FCSTD DOCUMENT  (FreeCAD 1.0R39319 (Git))
Label: session2_drawing4
License: All rights reserved
LicenseURL: https://en.wikipedia.org/wiki/All_rights_reserved
objects: Sketcher::SketchObject×1, PartDesign::Body×1
note: 3 computed .brp shape members not serialized (recipe doc carries the construction recipe); baked Part::Feature solids carry a one-line shape summary decoded from their .brp

FEATURE [Sketcher::SketchObject] Sketch
  ArcFitTolerance = 1e-06
  AttachmentSupport = -> [XY_Plane]
  FullyConstrained = true
  MakeInternals = false
  MapMode = 5
  sketch-geometry (32):
    g0: ArcOfCircle CenterX=-6.783e-13 CenterY=2.02e-13 CenterZ=0 NormalX=0 NormalY=0 NormalZ=1 AngleXU=0 Radius=55 StartAngle=1.75363 EndAngle=2.95876
    g1: ArcOfCircle CenterX=-113 CenterY=1.8543e-12 CenterZ=0 NormalX=0 NormalY=0 NormalZ=1 AngleXU=0 Radius=26 StartAngle=0.394791 EndAngle=5.88839
    g2: ArcOfCircle CenterX=113 CenterY=4.685e-13 CenterZ=0 NormalX=0 NormalY=0 NormalZ=1 AngleXU=0 Radius=26 StartAngle=3.53638 EndAngle=9.02999
    g3: ArcOfCircle CenterX=5.801e-13 CenterY=113 CenterZ=0 NormalX=0 NormalY=0 NormalZ=1 AngleXU=0 Radius=26 StartAngle=5.10718 EndAngle=10.6008
    g4: LineSegment StartX=-131.385 StartY=18.3848 StartZ=0 EndX=-18.3848 EndY=131.385 EndZ=0
    g5: LineSegment StartX=18.3848 StartY=131.385 StartZ=0 EndX=131.385 EndY=18.3848 EndZ=0
    g6: ArcOfCircle CenterX=8.066e-13 CenterY=-113 CenterZ=0 NormalX=0 NormalY=0 NormalZ=1 AngleXU=0 Radius=26 StartAngle=1.96559 EndAngle=7.45919
    g7: Circle [constr] CenterX=-6.783e-13 CenterY=2.02e-13 CenterZ=0 NormalX=0 NormalY=0 NormalZ=1 AngleXU=0 Radius=113
    g8: ArcOfCircle CenterX=-59.8055 CenterY=-85.0841 CenterZ=0 NormalX=0 NormalY=0 NormalZ=1 AngleXU=0 Radius=40 StartAngle=5.84647 EndAngle=7.24131
    g9: ArcOfCircle CenterX=-6.783e-13 CenterY=2.02e-13 CenterZ=0 NormalX=0 NormalY=0 NormalZ=1 AngleXU=0 Radius=64 StartAngle=3.75426 EndAngle=4.09972
    g10: ArcOfCircle CenterX=-85.0841 CenterY=-59.8055 CenterZ=0 NormalX=0 NormalY=0 NormalZ=1 AngleXU=0 Radius=40 StartAngle=0.612669 EndAngle=2.00752
    g11: ArcOfCircle CenterX=85.0841 CenterY=-59.8055 CenterZ=0 NormalX=0 NormalY=0 NormalZ=1 AngleXU=0 Radius=40 StartAngle=1.13408 EndAngle=2.52892
    g12: ArcOfCircle CenterX=-2.25532e-11 CenterY=-1.66575e-11 CenterZ=0 NormalX=0 NormalY=0 NormalZ=1 AngleXU=0 Radius=64 StartAngle=5.32506 EndAngle=5.67052
    g13: ArcOfCircle CenterX=59.8055 CenterY=-85.0841 CenterZ=0 NormalX=0 NormalY=0 NormalZ=1 AngleXU=0 Radius=40 StartAngle=2.18347 EndAngle=3.57831
    g14: Circle CenterX=-113 CenterY=1.8543e-12 CenterZ=0 NormalX=0 NormalY=0 NormalZ=1 AngleXU=0 Radius=4.751e-13
    g15: Circle CenterX=113 CenterY=4.685e-13 CenterZ=0 NormalX=0 NormalY=0 NormalZ=1 AngleXU=0 Radius=20
    g16: Circle CenterX=-113 CenterY=1.8543e-12 CenterZ=0 NormalX=0 NormalY=0 NormalZ=1 AngleXU=0 Radius=4.721e-13
    g17: Circle CenterX=5.801e-13 CenterY=113 CenterZ=0 NormalX=0 NormalY=0 NormalZ=1 AngleXU=0 Radius=20
    g18: Circle CenterX=-113 CenterY=1.8543e-12 CenterZ=0 NormalX=0 NormalY=0 NormalZ=1 AngleXU=0 Radius=20
    g19: Circle CenterX=8.066e-13 CenterY=-113 CenterZ=0 NormalX=0 NormalY=0 NormalZ=1 AngleXU=0 Radius=20
    g20: Circle CenterX=-2.25532e-11 CenterY=-1.66575e-11 CenterZ=0 NormalX=0 NormalY=0 NormalZ=1 AngleXU=0 Radius=44
    g21: LineSegment StartX=-95.6795 StartY=10 StartZ=0 EndX=-42.8486 EndY=10 EndZ=0
    g22: LineSegment StartX=-95.6795 StartY=-10 StartZ=0 EndX=-42.8486 EndY=-10 EndZ=0
    g23: LineSegment StartX=95.6795 StartY=-10 StartZ=0 EndX=42.8486 EndY=-10 EndZ=0
    g24: LineSegment StartX=95.6795 StartY=10 StartZ=0 EndX=42.8486 EndY=10 EndZ=0
    g25: LineSegment StartX=-10 StartY=95.6795 StartZ=0 EndX=-10 EndY=42.8486 EndZ=0
    g26: LineSegment StartX=10 StartY=95.6795 StartZ=0 EndX=10 EndY=42.8486 EndZ=0
    g27: LineSegment StartX=-10 StartY=-95.6795 StartZ=0 EndX=-10 EndY=-42.8486 EndZ=0
    g28: LineSegment StartX=10 StartY=-95.6795 StartZ=0 EndX=10 EndY=-42.8486 EndZ=0
    g29: ArcOfCircle CenterX=-6.783e-13 CenterY=2.02e-13 CenterZ=0 NormalX=0 NormalY=0 NormalZ=1 AngleXU=0 Radius=55 StartAngle=3.32443 EndAngle=4.52955
    g30: ArcOfCircle CenterX=-6.783e-13 CenterY=2.02e-13 CenterZ=0 NormalX=0 NormalY=0 NormalZ=1 AngleXU=0 Radius=55 StartAngle=0.182835 EndAngle=1.38796
    g31: ArcOfCircle CenterX=-6.783e-13 CenterY=2.02e-13 CenterZ=0 NormalX=0 NormalY=0 NormalZ=1 AngleXU=0 Radius=55 StartAngle=4.89522 EndAngle=6.10035
  constraints (97):
    c: Coincident(g0,g-1)
    c: PointOnObject(g1,g-1)
    c: PointOnObject(g2,g-1)
    c: PointOnObject(g3,g-2)
    c: Diameter(g1) = 52
    c: Diameter(g0) = 110
    c: DistanceX(g1,g-1) = 113
    c: Equal(g1,g3)
    c: Equal(g3,g2)
    c: DistanceX(g-1,g2) = 113
    c: Distance(g0,g3) = 113
    c: Tangent(g4,g1) = 1.5708
    c: Tangent(g4,g3) = 1.5708
    c: Tangent(g5,g3) = 1.5708
    c: PointOnObject(g6,g-2)
    c: Coincident(g7,g0)
    c: Diameter(g7) = 226
    c: DistanceY(g6,g0) = 113
    c: Equal(g1,g6)
    c: Tangent(g8,g9) = 1.5708
    c: Tangent(g9,g10) = 1.5708
    c: Radius(g8) = 40
    c: Radius(g10) = 40
    c: Tangent(g10,g1) = 1.5708
    c: Tangent(g8,g6) = 1.5708
    c: Coincident(g9,g0)
    c: Radius(g9) = 64
    c: Tangent(g5,g2) = 1.5708
    c: Radius(g11) = 40
    c: Tangent(g13,g12) = 1.5708
    c: Radius(g13) = 40
    c: Radius(g12) = 64
    c: Block(g11)
    c: Block(g12)
    c: Block(g13)
    c: Coincident(g14,g1)
    c: Tangent(g14,g7)
    c: Coincident(g15,g2)
    c: Coincident(g16,g1)
    c: Tangent(g16,g7)
    c: Coincident(g17,g3)
    c: Coincident(g18,g1)
    c: Diameter(g18) = 40
    c: Equal(g18,g17)
    c: Equal(g17,g15)
    c: Coincident(g19,g6)
    c: Diameter(g19) = 40
    c: Coincident(g20,g12)
    c: Diameter(g20) = 88
    c: PointOnObject(g21,g18)
    c: PointOnObject(g21,g20)
    c: Horizontal(g21)
    c: PointOnObject(g22,g18)
    c: PointOnObject(g22,g20)
    c: Horizontal(g22)
    c: Distance(g-1,g21) = 10
    c: Distance(g21,g22) = 20
    c: Horizontal(g24)
    c: Horizontal(g23)
    c: Distance(g24,g23) = 20
    c: Block(g24)
    c: Block(g23)
    c: PointOnObject(g1,g22)
    c: PointOnObject(g1,g21)
    c: PointOnObject(g2,g24)
    c: PointOnObject(g2,g23)
    c: PointOnObject(g25,g17)
    c: PointOnObject(g25,g20)
    c: PointOnObject(g26,g17)
    c: PointOnObject(g26,g20)
    c: Vertical(g26)
    c: Vertical(g25)
    c: Distance(g26,g25) = 20
    c: Distance(g-2,g25) = 10
    c: Vertical(g28)
    c: Vertical(g27)
    c: Distance(g28,g27) = 20
    c: Block(g27)
    c: Block(g28)
    c: PointOnObject(g6,g28)
    c: PointOnObject(g6,g27)
    c: PointOnObject(g3,g25)
    c: PointOnObject(g3,g26)
    c: PointOnObject(g30,g26)
    c: PointOnObject(g0,g25)
    c: Equal(g0,g29)
    c: PointOnObject(g0,g21)
    c: PointOnObject(g29,g22)
    c: Coincident(g0,g29)
    c: Equal(g29,g30)
    c: PointOnObject(g31,g23)
    c: PointOnObject(g30,g24)
    c: Coincident(g29,g30)
    c: Equal(g29,g31)
    c: PointOnObject(g29,g27)
    c: PointOnObject(g31,g28)
    c: Coincident(g29,g31)
FEATURE [PartDesign::Body] Body
  AllowCompound = false
  Group = -> [Sketch]
  Origin = -> Origin
